# Revit family: heroal VS Z - Partly Integrated - Multi-Part - Middle Component
name_source: partatom
category: Fenster
revit_build: Autodesk Revit 2017 (Build: 20160225_1515(x64)
units: mm (PartAtom-declared; Revit-internal decimal feet)

## family parameters
Arbeitsebenenbasiert = Ja
Beim Laden mit Abzugskörper schneiden = Nein
Gemeinsam genutzt = Nein
Immer vertikal = Nein
OmniClass-Nummer = 23.30.60.11.11.17.14
OmniClass-Titel = Powered Awnings
Raumberechnungspunkt = Nein

## types (1)
- Middle Component
    Analytische Konstruktion = <None>
    Ballproof DIN EN 18032-3 = Requirement fulfilled
    Baugruppenkennzeichen = B2020110
    Beschreibung = heroal VS-Z Shading Systems
    Class according to DIN EN 14501 = 2-4
    Cover Type 1 = Cover : FME 45°
    Cover Type 2 = Cover : FME 90°
    Cover Type 3 = Cover : FME HC
    Edition number = 1
    Hersteller = heroal
    Light transmission level DIN EN 40010 = 3-20
    Material = fibreglass/PVC/polyester
    Max Height = max. 3 metres
    Max Width = max. 5 metres
    Modell = heroal VS-Z Shading Systems, Partly Integrated
    Summer heat protection [Gtot] = 0,06-0,25
    URL = http://www.heroal.com
    Vorgabe-Ansicht = 1219 mm
    Wind Load Resistance DIN EN 13561 = 6

## geometry (parser evidence)
native form markers: Sweep x9
no freeform markers — native parametric forms only
